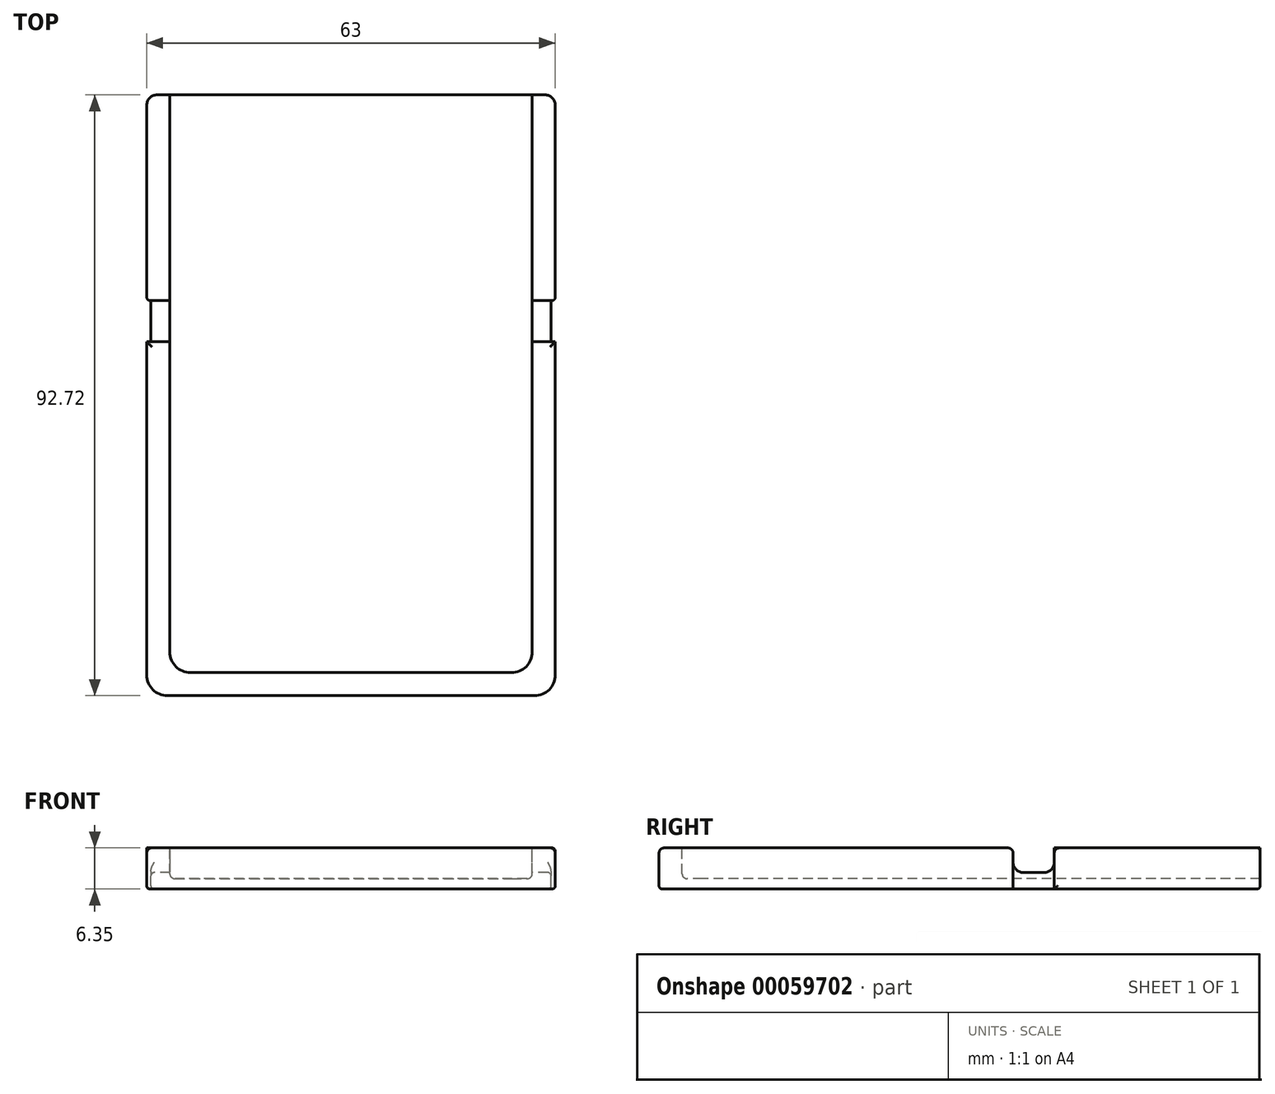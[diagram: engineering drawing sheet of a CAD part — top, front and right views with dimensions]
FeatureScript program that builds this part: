
annotation { "Feature Type Name" : "Feature", "Feature Type Description" : "" }
export const myFeature = defineFeature(function(context is Context, id is Id, definition is map)
    precondition{}
    {
        {
            var Q0;
            Q0=qCreatedBy(makeId("Top.planeOp"),FACE);
            var sketch = newSketch(context, id + "F0", { "sketchPlane" : qUnion([Q0])});
            skLineSegment(sketch, "E0.rect.bottom", {"start": v(28.32, -46.36) * mm, "end": v(-28.32, -46.36) * mm});
            skLineSegment(sketch, "E0.rect.top", {"start": v(29.9, 46.35) * mm, "end": v(-29.9, 46.35) * mm});
            skLineSegment(sketch, "E0.rect.left", {"start": v(31.5, -43.18) * mm, "end": v(31.5, 44.77) * mm});
            skLineSegment(sketch, "E0.rect.right", {"start": v(-31.5, -43.18) * mm, "end": v(-31.5, 44.77) * mm});
            skPoint(sketch, "E0.rect.middle", {"position": v(0, 0) * mm});
            skPoint(sketch, "E1.visualSharp", {"position": v(-31.5, -46.36) * mm});
            skArc(sketch, "E1.filletArc", {"start": v(-31.5, -43.18) * mm, "mid": v(-30.57, -45.43) * mm, "end": v(-28.32, -46.36) * mm});
            skPoint(sketch, "E2.visualSharp", {"position": v(31.5, -46.36) * mm});
            skArc(sketch, "E2.filletArc", {"start": v(28.32, -46.36) * mm, "mid": v(30.57, -45.43) * mm, "end": v(31.5, -43.18) * mm});
            skPoint(sketch, "E3.visualSharp", {"position": v(-31.5, 46.35) * mm});
            skArc(sketch, "E3.filletArc", {"start": v(-29.9, 46.35) * mm, "mid": v(-31.03, 45.9) * mm, "end": v(-31.5, 44.77) * mm});
            skPoint(sketch, "E4.visualSharp", {"position": v(31.5, 46.35) * mm});
            skArc(sketch, "E4.filletArc", {"start": v(31.5, 44.77) * mm, "mid": v(31.03, 45.9) * mm, "end": v(29.9, 46.36) * mm});
            skSolve(sketch);
        }
        {
            var Q0;
            Q0=makeQuery(id+"F0.imprint","IMPRINT",FACE,{"disambiguationData":[TD([[makeQuery(id+"F0.imprint","IMPRINT",EDGE,{"derivedFrom":sQuery(id+"F0.wireOp",EDGE,"E0.rect.bottom")}),-1.0]])]});
            extrude(context, id + "F9", {"entities" : qUnion([Q0]), "depth" : 6.35 * mm});
        }
        {
            var Q0;
            Q0=makeQuery(id+"F9.opExtrude","CAP_FACE",FACE,{"disambiguationData":[OSD([sQuery(id+"F0.wireOp",EDGE,"E0.rect.bottom"),sQuery(id+"F0.wireOp",EDGE,"E0.rect.top"),sQuery(id+"F0.wireOp",EDGE,"E0.rect.left"),sQuery(id+"F0.wireOp",EDGE,"E0.rect.right")])],"isStart":false});
            var sketch = newSketch(context, id + "F1", { "sketchPlane" : qUnion([Q0])});
            skLineSegment(sketch, "E5", {"start": v(-27.94, 46.36) * mm, "end": v(-27.94, -39.62) * mm});
            skLineSegment(sketch, "E6", {"start": v(-24.77, -42.8) * mm, "end": v(24.77, -42.8) * mm});
            skLineSegment(sketch, "E7", {"start": v(27.94, -39.62) * mm, "end": v(27.94, 46.36) * mm});
            skLineSegment(sketch, "E8", {"start": v(0, 46.35) * mm, "end": v(0, 0) * mm, "construction": true});
            skPoint(sketch, "E9.visualSharp", {"position": v(-27.94, -42.8) * mm});
            skArc(sketch, "E9.filletArc", {"start": v(-27.94, -39.62) * mm, "mid": v(-27.01, -41.87) * mm, "end": v(-24.77, -42.8) * mm});
            skPoint(sketch, "E10.visualSharp", {"position": v(27.94, -42.8) * mm});
            skArc(sketch, "E10.filletArc", {"start": v(24.77, -42.8) * mm, "mid": v(27.01, -41.87) * mm, "end": v(27.94, -39.62) * mm});
            skLineSegment(sketch, "E11", {"start": v(-27.94, 46.36) * mm, "end": v(27.94, 46.36) * mm});
            skSolve(sketch);
        }
        {
            var Q0;
            Q0 = qSketchRegion(id + "F1", true);
            extrude(context, id + "F2", {"entities" : qUnion([Q0]), "operationType" : NewBodyOperationType.REMOVE, "oppositeDirection" : true, "depth" : 4.76 * mm});
        }
        {
            var Q0;
            Q0=qCreatedBy(makeId("Right.planeOp"),FACE);
            var sketch = newSketch(context, id + "F3", { "sketchPlane" : qUnion([Q0])});
            skLineSegment(sketch, "E12.bottom", {"start": v(8.26, 6.35) * mm, "end": v(14.6, 6.35) * mm});
            skLineSegment(sketch, "E12.top", {"start": v(9.84, 2.54) * mm, "end": v(13.02, 2.54) * mm});
            skLineSegment(sketch, "E12.left", {"start": v(8.26, 6.35) * mm, "end": v(8.26, 4.13) * mm});
            skLineSegment(sketch, "E12.right", {"start": v(14.6, 6.35) * mm, "end": v(14.6, 4.13) * mm});
            skPoint(sketch, "E13.visualSharp", {"position": v(8.26, 2.54) * mm});
            skArc(sketch, "E13.filletArc", {"start": v(8.26, 4.13) * mm, "mid": v(8.72, 3) * mm, "end": v(9.84, 2.54) * mm});
            skPoint(sketch, "E14.visualSharp", {"position": v(14.6, 2.54) * mm});
            skArc(sketch, "E14.filletArc", {"start": v(13.02, 2.54) * mm, "mid": v(14.14, 3) * mm, "end": v(14.6, 4.13) * mm});
            skSolve(sketch);
        }
        {
            var Q0;
            Q0 = qSketchRegion(id + "F3", true);
            extrude(context, id + "F4", {"entities" : qUnion([Q0]), "operationType" : NewBodyOperationType.REMOVE, "endBound" : BoundingType.SYMMETRIC, "depth" : 76.2 * mm});
        }
        {
            var Q0;
            {var subQ0=sQuery(id+"F0.wireOp",EDGE,"E2.filletArc");var subQ1=sQuery(id+"F0.wireOp",EDGE,"E0.rect.bottom");var subQ2=sQuery(id+"F0.wireOp",EDGE,"E0.rect.left");var subQ3=sQuery(id+"F0.wireOp",EDGE,"E0.rect.right");var subQ4=sQuery(id+"F0.wireOp",EDGE,"E1.filletArc");Q0=makeQuery(id+"F4.boolean.opBoolean","SPLIT",FACE,{"disambiguationData":[TD([makeQuery(id+"F9.opExtrude","SWEPT_FACE",FACE,{"disambiguationData":[OSD([subQ1])]})])],"derivedFrom":makeQuery(id+"F9.opExtrude","CAP_FACE",FACE,{"disambiguationData":[OSD([subQ1,sQuery(id+"F0.wireOp",EDGE,"E0.rect.top"),subQ2,subQ3,subQ4,subQ0,sQuery(id+"F0.wireOp",EDGE,"E3.filletArc"),sQuery(id+"F0.wireOp",EDGE,"E4.filletArc")])],"isStart":false})});}
            var sketch = newSketch(context, id + "F5", { "sketchPlane" : qUnion([Q0])});
            skLineSegment(sketch, "E15.bottom", {"start": v(-31.5, 8.26) * mm, "end": v(-30.86, 8.26) * mm});
            skLineSegment(sketch, "E15.top", {"start": v(-31.5, 14.6) * mm, "end": v(-30.86, 14.6) * mm});
            skLineSegment(sketch, "E15.left", {"start": v(-31.5, 8.26) * mm, "end": v(-31.5, 14.6) * mm});
            skLineSegment(sketch, "E15.right", {"start": v(-30.86, 8.26) * mm, "end": v(-30.86, 14.6) * mm});
            skLineSegment(sketch, "E16.MirrorCS", {"start": v(31.5, 8.26) * mm, "end": v(30.86, 8.26) * mm});
            skLineSegment(sketch, "E17.MirrorCS", {"start": v(31.5, 14.6) * mm, "end": v(30.86, 14.6) * mm});
            skLineSegment(sketch, "E18.MirrorCS", {"start": v(30.86, 8.26) * mm, "end": v(30.86, 14.6) * mm});
            skLineSegment(sketch, "E19.MirrorCS", {"start": v(31.5, 8.26) * mm, "end": v(31.5, 14.6) * mm});
            skSolve(sketch);
        }
        {
            var Q0;
            Q0 = qSketchRegion(id + "F5", true);
            extrude(context, id + "F6", {"entities" : qUnion([Q0]), "operationType" : NewBodyOperationType.REMOVE, "endBound" : BoundingType.THROUGH_ALL, "oppositeDirection" : true, "depth" : 25.4 * mm});
        }
        {
            var Q0;
            Q0=makeQuery(id+"F2.boolean.opBoolean","COPY",EDGE,{"derivedFrom":makeQuery(id+"F2.opExtrude","CAP_EDGE",EDGE,{"disambiguationData":[OSD([sQuery(id+"F1.wireOp",EDGE,"E7")])],"isStart":false})});
            var Q1;
            {var subQ0=sQuery(id+"F0.wireOp",EDGE,"E0.rect.top");var subQ1=sQuery(id+"F1.wireOp",EDGE,"E7");Q1=makeQuery(id+"F4.boolean.opBoolean","SPLIT",EDGE,{"disambiguationData":[TD([makeQuery(id+"F9.opExtrude","SWEPT_FACE",FACE,{"disambiguationData":[OSD([subQ0])]})])],"derivedFrom":makeQuery(id+"F2.boolean.opBoolean","COPY",EDGE,{"derivedFrom":makeQuery(id+"F2.opExtrude","CAP_EDGE",EDGE,{"disambiguationData":[OSD([subQ1])],"isStart":true})})});}
            var Q2;
            {var subQ0=sQuery(id+"F1.wireOp",EDGE,"E7");Q2=makeQuery(id+"F4.boolean.opBoolean","SPLIT",EDGE,{"disambiguationData":[TD([makeQuery(id+"F2.boolean.opBoolean","COPY",FACE,{"derivedFrom":makeQuery(id+"F2.opExtrude","SWEPT_FACE",FACE,{"disambiguationData":[OSD([sQuery(id+"F1.wireOp",EDGE,"E10.filletArc")])]})})])],"derivedFrom":makeQuery(id+"F2.boolean.opBoolean","COPY",EDGE,{"derivedFrom":makeQuery(id+"F2.opExtrude","CAP_EDGE",EDGE,{"disambiguationData":[OSD([subQ0])],"isStart":true})})});}
            var Q3;
            {var subQ0=sQuery(id+"F0.wireOp",EDGE,"E0.rect.top");var subQ1=sQuery(id+"F1.wireOp",EDGE,"E5");Q3=makeQuery(id+"F4.boolean.opBoolean","SPLIT",EDGE,{"disambiguationData":[TD([makeQuery(id+"F9.opExtrude","SWEPT_FACE",FACE,{"disambiguationData":[OSD([subQ0])]})])],"derivedFrom":makeQuery(id+"F2.boolean.opBoolean","COPY",EDGE,{"derivedFrom":makeQuery(id+"F2.opExtrude","CAP_EDGE",EDGE,{"disambiguationData":[OSD([subQ1])],"isStart":true})})});}
            var Q4;
            {var subQ0=sQuery(id+"F0.wireOp",EDGE,"E0.rect.right");var subQ1=sQuery(id+"F0.wireOp",EDGE,"E0.rect.top");Q4=makeQuery(id+"F4.boolean.opBoolean","SPLIT",EDGE,{"disambiguationData":[TD([makeQuery(id+"F9.opExtrude","SWEPT_FACE",FACE,{"disambiguationData":[OSD([subQ1])]})])],"derivedFrom":makeQuery(id+"F9.opExtrude","CAP_EDGE",EDGE,{"disambiguationData":[OSD([subQ0])],"isStart":false})});}
            var Q5;
            {var subQ0=sQuery(id+"F0.wireOp",EDGE,"E1.filletArc");var subQ1=sQuery(id+"F0.wireOp",EDGE,"E0.rect.right");Q5=makeQuery(id+"F4.boolean.opBoolean","SPLIT",EDGE,{"disambiguationData":[TD([makeQuery(id+"F9.opExtrude","SWEPT_FACE",FACE,{"disambiguationData":[OSD([subQ0])]})])],"derivedFrom":makeQuery(id+"F9.opExtrude","CAP_EDGE",EDGE,{"disambiguationData":[OSD([subQ1])],"isStart":false})});}
            var Q6;
            {var subQ0=sQuery(id+"F0.wireOp",EDGE,"E0.rect.left");var subQ1=sQuery(id+"F0.wireOp",EDGE,"E0.rect.top");Q6=makeQuery(id+"F4.boolean.opBoolean","SPLIT",EDGE,{"disambiguationData":[TD([makeQuery(id+"F9.opExtrude","SWEPT_FACE",FACE,{"disambiguationData":[OSD([subQ1])]})])],"derivedFrom":makeQuery(id+"F9.opExtrude","CAP_EDGE",EDGE,{"disambiguationData":[OSD([subQ0])],"isStart":false})});}
            var Q7;
            {var subQ0=sQuery(id+"F0.wireOp",EDGE,"E0.rect.right");var subQ1=sQuery(id+"F0.wireOp",EDGE,"E0.rect.top");Q7=makeQuery(id+"F2.boolean.opBoolean","SPLIT",EDGE,{"disambiguationData":[TD([makeQuery(id+"F9.opExtrude","SWEPT_FACE",FACE,{"disambiguationData":[OSD([subQ0])]})])],"derivedFrom":makeQuery(id+"F9.opExtrude","CAP_EDGE",EDGE,{"disambiguationData":[OSD([subQ1])],"isStart":false})});}
            var Q8;
            {var subQ0=sQuery(id+"F0.wireOp",EDGE,"E0.rect.left");var subQ1=sQuery(id+"F0.wireOp",EDGE,"E0.rect.top");Q8=makeQuery(id+"F2.boolean.opBoolean","SPLIT",EDGE,{"disambiguationData":[TD([makeQuery(id+"F9.opExtrude","SWEPT_FACE",FACE,{"disambiguationData":[OSD([subQ0])]})])],"derivedFrom":makeQuery(id+"F9.opExtrude","CAP_EDGE",EDGE,{"disambiguationData":[OSD([subQ1])],"isStart":false})});}
            var Q9;
            Q9=makeQuery(id+"F4.boolean.opBoolean","COPY",EDGE,{"disambiguationData":[OD(1.0)],"derivedFrom":makeQuery(id+"F4.opExtrude","SWEPT_EDGE",EDGE,{"disambiguationData":[OSD([sQuery(id+"F3.wireOp",EDGE,"E12.bottom"),sQuery(id+"F3.wireOp",EDGE,"E12.right")])]})});
            var Q10;
            Q10=makeQuery(id+"F4.boolean.opBoolean","COPY",EDGE,{"disambiguationData":[OD(1.0)],"derivedFrom":makeQuery(id+"F4.opExtrude","SWEPT_EDGE",EDGE,{"disambiguationData":[OSD([sQuery(id+"F3.wireOp",EDGE,"E12.bottom"),sQuery(id+"F3.wireOp",EDGE,"E12.left")])]})});
            var Q11;
            Q11=makeQuery(id+"F4.boolean.opBoolean","COPY",EDGE,{"disambiguationData":[OD(0.0)],"derivedFrom":makeQuery(id+"F4.opExtrude","SWEPT_EDGE",EDGE,{"disambiguationData":[OSD([sQuery(id+"F3.wireOp",EDGE,"E12.bottom"),sQuery(id+"F3.wireOp",EDGE,"E12.right")])]})});
            var Q12;
            Q12=makeQuery(id+"F4.boolean.opBoolean","COPY",EDGE,{"disambiguationData":[OD(0.0)],"derivedFrom":makeQuery(id+"F4.opExtrude","SWEPT_EDGE",EDGE,{"disambiguationData":[OSD([sQuery(id+"F3.wireOp",EDGE,"E12.bottom"),sQuery(id+"F3.wireOp",EDGE,"E12.left")])]})});
            var Q13;
            Q13=makeQuery(id+"F2.boolean.opBoolean","COPY",EDGE,{"derivedFrom":makeQuery(id+"F2.opExtrude","CAP_EDGE",EDGE,{"disambiguationData":[OSD([sQuery(id+"F1.wireOp",EDGE,"E11")])],"isStart":false})});
            var Q14;
            Q14=makeQuery(id+"F4.boolean.opBoolean","INTERSECT",EDGE,{"derivedFrom":[makeQuery(id+"F9.opExtrude","SWEPT_FACE",FACE,{"disambiguationData":[OSD([sQuery(id+"F0.wireOp",EDGE,"E0.rect.right")])]}),makeQuery(id+"F4.opExtrude","SWEPT_FACE",FACE,{"disambiguationData":[OSD([sQuery(id+"F3.wireOp",EDGE,"E12.top")])]})]});
            var Q15;
            Q15=makeQuery(id+"F4.boolean.opBoolean","INTERSECT",EDGE,{"derivedFrom":[makeQuery(id+"F9.opExtrude","SWEPT_FACE",FACE,{"disambiguationData":[OSD([sQuery(id+"F0.wireOp",EDGE,"E0.rect.left")])]}),makeQuery(id+"F4.opExtrude","SWEPT_FACE",FACE,{"disambiguationData":[OSD([sQuery(id+"F3.wireOp",EDGE,"E12.top")])]})]});
            fillet(context, id + "F7", {"entities" : qUnion([Q0, Q1, Q2, Q3, Q4, Q5, Q6, Q7, Q8, Q9, Q10, Q11, Q12, Q13, Q14, Q15]), "radius" : 0.8 * mm, "tangentPropagation" : true, "allowEdgeOverflow" : false});
        }
        {
            var Q0;
            Q0=makeQuery(id+"F6.boolean.opBoolean","MERGE",EDGE,{"derivedFrom":[makeQuery(id+"F4.boolean.opBoolean","INTERSECT",EDGE,{"derivedFrom":[makeQuery(id+"F9.opExtrude","SWEPT_FACE",FACE,{"disambiguationData":[OSD([sQuery(id+"F0.wireOp",EDGE,"E0.rect.right")])]}),makeQuery(id+"F4.opExtrude","SWEPT_FACE",FACE,{"disambiguationData":[OSD([sQuery(id+"F3.wireOp",EDGE,"E12.right")])]})]}),makeQuery(id+"F6.opExtrude","SWEPT_EDGE",EDGE,{"disambiguationData":[OSD([sQuery(id+"F5.wireOp",EDGE,"E15.top"),sQuery(id+"F5.wireOp",EDGE,"E15.left")])]})]});
            var Q1;
            {var subQ0=sQuery(id+"F0.wireOp",EDGE,"E0.rect.right");Q1=makeQuery(id+"F6.boolean.opBoolean","MERGE",EDGE,{"derivedFrom":[makeQuery(id+"F4.boolean.opBoolean","INTERSECT",EDGE,{"derivedFrom":[makeQuery(id+"F9.opExtrude","SWEPT_FACE",FACE,{"disambiguationData":[OSD([subQ0])]}),makeQuery(id+"F4.opExtrude","SWEPT_FACE",FACE,{"disambiguationData":[OSD([sQuery(id+"F3.wireOp",EDGE,"E12.left")])]})]}),makeQuery(id+"F6.opExtrude","SWEPT_EDGE",EDGE,{"disambiguationData":[OSD([subQ0,sQuery(id+"F5.wireOp",EDGE,"E15.bottom"),sQuery(id+"F5.wireOp",EDGE,"E15.left")])]})]});}
            var Q2;
            Q2=makeQuery(id+"F6.boolean.opBoolean","MERGE",EDGE,{"derivedFrom":[makeQuery(id+"F4.boolean.opBoolean","INTERSECT",EDGE,{"derivedFrom":[makeQuery(id+"F9.opExtrude","SWEPT_FACE",FACE,{"disambiguationData":[OSD([sQuery(id+"F0.wireOp",EDGE,"E0.rect.left")])]}),makeQuery(id+"F4.opExtrude","SWEPT_FACE",FACE,{"disambiguationData":[OSD([sQuery(id+"F3.wireOp",EDGE,"E12.right")])]})]}),makeQuery(id+"F6.opExtrude","SWEPT_EDGE",EDGE,{"disambiguationData":[OSD([sQuery(id+"F5.wireOp",EDGE,"E17.MirrorCS"),sQuery(id+"F5.wireOp",EDGE,"E19.MirrorCS")])]})]});
            var Q3;
            {var subQ0=sQuery(id+"F0.wireOp",EDGE,"E0.rect.left");Q3=makeQuery(id+"F6.boolean.opBoolean","MERGE",EDGE,{"derivedFrom":[makeQuery(id+"F4.boolean.opBoolean","INTERSECT",EDGE,{"derivedFrom":[makeQuery(id+"F9.opExtrude","SWEPT_FACE",FACE,{"disambiguationData":[OSD([subQ0])]}),makeQuery(id+"F4.opExtrude","SWEPT_FACE",FACE,{"disambiguationData":[OSD([sQuery(id+"F3.wireOp",EDGE,"E12.left")])]})]}),makeQuery(id+"F6.opExtrude","SWEPT_EDGE",EDGE,{"disambiguationData":[OSD([subQ0,sQuery(id+"F5.wireOp",EDGE,"E16.MirrorCS"),sQuery(id+"F5.wireOp",EDGE,"E19.MirrorCS")])]})]});}
            var Q4;
            Q4=makeQuery(id+"F6.boolean.opBoolean","INTERSECT",EDGE,{"derivedFrom":[makeQuery(id+"F9.opExtrude","CAP_FACE",FACE,{"disambiguationData":[OSD([sQuery(id+"F0.wireOp",EDGE,"E0.rect.bottom"),sQuery(id+"F0.wireOp",EDGE,"E0.rect.top"),sQuery(id+"F0.wireOp",EDGE,"E0.rect.left"),sQuery(id+"F0.wireOp",EDGE,"E0.rect.right"),sQuery(id+"F0.wireOp",EDGE,"E1.filletArc"),sQuery(id+"F0.wireOp",EDGE,"E2.filletArc"),sQuery(id+"F0.wireOp",EDGE,"E3.filletArc"),sQuery(id+"F0.wireOp",EDGE,"E4.filletArc")])],"isStart":true}),makeQuery(id+"F6.opExtrude","SWEPT_FACE",FACE,{"disambiguationData":[OSD([sQuery(id+"F5.wireOp",EDGE,"E18.MirrorCS")])]})]});
            var Q5;
            Q5=makeQuery(id+"F6.boolean.opBoolean","INTERSECT",EDGE,{"derivedFrom":[makeQuery(id+"F4.boolean.opBoolean","COPY",FACE,{"disambiguationData":[OD(1.0)],"derivedFrom":makeQuery(id+"F4.opExtrude","SWEPT_FACE",FACE,{"disambiguationData":[OSD([sQuery(id+"F3.wireOp",EDGE,"E12.top")])]})}),makeQuery(id+"F6.opExtrude","SWEPT_FACE",FACE,{"disambiguationData":[OSD([sQuery(id+"F5.wireOp",EDGE,"E15.right")])]})]});
            var Q6;
            Q6=makeQuery(id+"F6.boolean.opBoolean","INTERSECT",EDGE,{"derivedFrom":[makeQuery(id+"F4.boolean.opBoolean","COPY",FACE,{"disambiguationData":[OD(0.0)],"derivedFrom":makeQuery(id+"F4.opExtrude","SWEPT_FACE",FACE,{"disambiguationData":[OSD([sQuery(id+"F3.wireOp",EDGE,"E12.top")])]})}),makeQuery(id+"F6.opExtrude","SWEPT_FACE",FACE,{"disambiguationData":[OSD([sQuery(id+"F5.wireOp",EDGE,"E18.MirrorCS")])]})]});
            var Q7;
            Q7=makeQuery(id+"F6.boolean.opBoolean","INTERSECT",EDGE,{"derivedFrom":[makeQuery(id+"F9.opExtrude","CAP_FACE",FACE,{"disambiguationData":[OSD([sQuery(id+"F0.wireOp",EDGE,"E0.rect.bottom"),sQuery(id+"F0.wireOp",EDGE,"E0.rect.top"),sQuery(id+"F0.wireOp",EDGE,"E0.rect.left"),sQuery(id+"F0.wireOp",EDGE,"E0.rect.right"),sQuery(id+"F0.wireOp",EDGE,"E1.filletArc"),sQuery(id+"F0.wireOp",EDGE,"E2.filletArc"),sQuery(id+"F0.wireOp",EDGE,"E3.filletArc"),sQuery(id+"F0.wireOp",EDGE,"E4.filletArc")])],"isStart":true}),makeQuery(id+"F6.opExtrude","SWEPT_FACE",FACE,{"disambiguationData":[OSD([sQuery(id+"F5.wireOp",EDGE,"E15.right")])]})]});
            var Q8;
            {var subQ0=sQuery(id+"F0.wireOp",EDGE,"E3.filletArc");var subQ1=sQuery(id+"F0.wireOp",EDGE,"E0.rect.right");Q8=makeQuery(id+"F6.boolean.opBoolean","SPLIT",EDGE,{"disambiguationData":[TD([makeQuery(id+"F9.opExtrude","SWEPT_FACE",FACE,{"disambiguationData":[OSD([subQ0])]})])],"derivedFrom":makeQuery(id+"F9.opExtrude","CAP_EDGE",EDGE,{"disambiguationData":[OSD([subQ1])],"isStart":true})});}
            var Q9;
            {var subQ0=sQuery(id+"F0.wireOp",EDGE,"E1.filletArc");var subQ1=sQuery(id+"F0.wireOp",EDGE,"E0.rect.right");Q9=makeQuery(id+"F6.boolean.opBoolean","SPLIT",EDGE,{"disambiguationData":[TD([makeQuery(id+"F9.opExtrude","SWEPT_FACE",FACE,{"disambiguationData":[OSD([subQ0])]})])],"derivedFrom":makeQuery(id+"F9.opExtrude","CAP_EDGE",EDGE,{"disambiguationData":[OSD([subQ1])],"isStart":true})});}
            var Q10;
            {var subQ0=sQuery(id+"F0.wireOp",EDGE,"E0.rect.left");var subQ1=sQuery(id+"F0.wireOp",EDGE,"E2.filletArc");Q10=makeQuery(id+"F6.boolean.opBoolean","SPLIT",EDGE,{"disambiguationData":[TD([makeQuery(id+"F9.opExtrude","SWEPT_FACE",FACE,{"disambiguationData":[OSD([subQ1])]})])],"derivedFrom":makeQuery(id+"F9.opExtrude","CAP_EDGE",EDGE,{"disambiguationData":[OSD([subQ0])],"isStart":true})});}
            var Q11;
            Q11=makeQuery(id+"F9.opExtrude","CAP_EDGE",EDGE,{"disambiguationData":[OSD([sQuery(id+"F0.wireOp",EDGE,"E0.rect.bottom")])],"isStart":true});
            var Q12;
            {var subQ0=sQuery(id+"F0.wireOp",EDGE,"E4.filletArc");var subQ1=sQuery(id+"F0.wireOp",EDGE,"E0.rect.left");Q12=makeQuery(id+"F6.boolean.opBoolean","SPLIT",EDGE,{"disambiguationData":[TD([makeQuery(id+"F9.opExtrude","SWEPT_FACE",FACE,{"disambiguationData":[OSD([subQ0])]})])],"derivedFrom":makeQuery(id+"F9.opExtrude","CAP_EDGE",EDGE,{"disambiguationData":[OSD([subQ1])],"isStart":true})});}
            fillet(context, id + "F8", {"entities" : qUnion([Q0, Q1, Q2, Q3, Q4, Q5, Q6, Q7, Q8, Q9, Q10, Q11, Q12]), "radius" : 0.5 * mm, "tangentPropagation" : true, "allowEdgeOverflow" : false});
        }
    });
